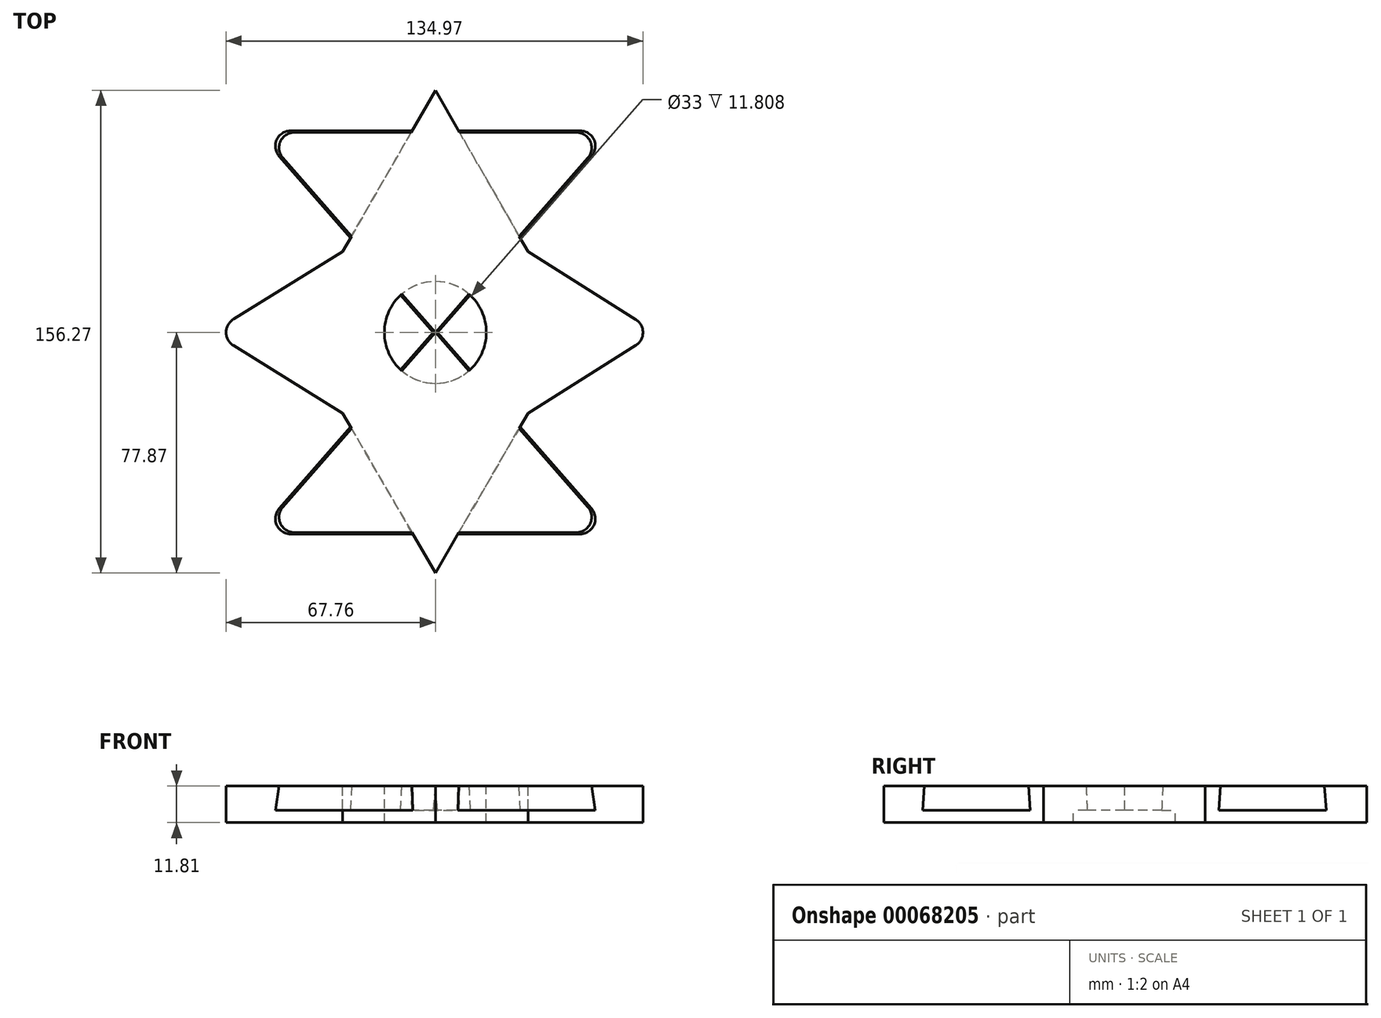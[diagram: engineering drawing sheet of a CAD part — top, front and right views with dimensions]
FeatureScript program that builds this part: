
annotation { "Feature Type Name" : "Feature", "Feature Type Description" : "" }
export const myFeature = defineFeature(function(context is Context, id is Id, definition is map)
    precondition{}
    {
        {
            var Q0;
            Q0=qCreatedBy(makeId("Top.planeOp"),FACE);
            var sketch = newSketch(context, id + "F0", { "sketchPlane" : qUnion([Q0])});
            skLineSegment(sketch, "E0.bottom", {"start": v(-30, 26.17) * mm, "end": v(30, 26.17) * mm});
            skLineSegment(sketch, "E0.top", {"start": v(-30, -26.17) * mm, "end": v(30, -26.17) * mm});
            skLineSegment(sketch, "E0.left", {"start": v(-30, 26.17) * mm, "end": v(-30, -26.17) * mm});
            skLineSegment(sketch, "E0.right", {"start": v(30, 26.17) * mm, "end": v(30, -26.17) * mm});
            skPoint(sketch, "E0.middle", {"position": v(0, 0) * mm});
            skLineSegment(sketch, "E1", {"start": v(-30, 26.17) * mm, "end": v(0, 78.4) * mm});
            skLineSegment(sketch, "E2", {"start": v(0, 78.4) * mm, "end": v(30, 26.17) * mm});
            skLineSegment(sketch, "E3", {"start": v(30, 26.17) * mm, "end": v(71.6, 0) * mm});
            skLineSegment(sketch, "E4", {"start": v(71.6, 0) * mm, "end": v(30, -26.17) * mm});
            skLineSegment(sketch, "E5", {"start": v(-30, -26.17) * mm, "end": v(-72.26, 0) * mm});
            skLineSegment(sketch, "E6", {"start": v(-72.26, 0) * mm, "end": v(-30, 26.17) * mm});
            skLineSegment(sketch, "E7", {"start": v(-30, -26.17) * mm, "end": v(0, -77.87) * mm});
            skLineSegment(sketch, "E8", {"start": v(0, -77.87) * mm, "end": v(30, -26.17) * mm});
            skCircle(sketch, "E9", {"center": v(0, 0) * mm, "radius": 16.5 * mm});
            skSolve(sketch);
        }
        {
            var Q0;
            Q0 = qSketchRegion(id + "F0", true);
            extrude(context, id + "F1", {"entities" : qUnion([Q0]), "oppositeDirection" : true, "depth" : 11.8 * mm});
        }
        {
            var Q0;
            Q0=qCreatedBy(makeId("Top.planeOp"),FACE);
            var sketch = newSketch(context, id + "F2", { "sketchPlane" : qUnion([Q0])});
            skLineSegment(sketch, "E10", {"start": v(0, 0) * mm, "end": v(-56.59, 64.76) * mm});
            skLineSegment(sketch, "E11", {"start": v(-56.59, 64.76) * mm, "end": v(56.59, 64.76) * mm});
            skLineSegment(sketch, "E12", {"start": v(56.59, 64.76) * mm, "end": v(0, 0) * mm});
            skLineSegment(sketch, "E13", {"start": v(0, 0) * mm, "end": v(-56.59, -64.76) * mm});
            skLineSegment(sketch, "E14", {"start": v(-56.59, -64.76) * mm, "end": v(56.59, -64.76) * mm});
            skLineSegment(sketch, "E15", {"start": v(56.59, -64.76) * mm, "end": v(0, 0) * mm});
            skSolve(sketch);
        }
        {
            var Q0;
            Q0=makeQuery(id+"F2.imprint","IMPRINT",FACE,{"disambiguationData":[TD([[makeQuery(id+"F2.imprint","IMPRINT",EDGE,{"derivedFrom":sQuery(id+"F2.wireOp",EDGE,"E13")}),1.0]])]});
            var Q1;
            Q1=makeQuery(id+"F2.imprint","IMPRINT",FACE,{"disambiguationData":[TD([[makeQuery(id+"F2.imprint","IMPRINT",EDGE,{"derivedFrom":sQuery(id+"F2.wireOp",EDGE,"E10")}),-1.0]])]});
            extrude(context, id + "F3", {"entities" : qUnion([Q0, Q1]), "operationType" : NewBodyOperationType.ADD, "oppositeDirection" : true, "depth" : 7.77 * mm, "hasDraft" : true, "draftAngle" : 4 * degree});
        }
        {
            var Q0;
            Q0=makeQuery(id+"F3.opExtrude","SWEPT_EDGE",EDGE,{"disambiguationData":[OSD([sQuery(id+"F2.wireOp",EDGE,"E10"),sQuery(id+"F2.wireOp",EDGE,"E11")])]});
            var Q1;
            Q1=makeQuery(id+"F1.opExtrude","SWEPT_EDGE",EDGE,{"disambiguationData":[OSD([sQuery(id+"F0.wireOp",EDGE,"E5"),sQuery(id+"F0.wireOp",EDGE,"E6")])]});
            var Q2;
            Q2=makeQuery(id+"F3.opExtrude","SWEPT_EDGE",EDGE,{"disambiguationData":[OSD([sQuery(id+"F2.wireOp",EDGE,"E13"),sQuery(id+"F2.wireOp",EDGE,"E14")])]});
            fillet(context, id + "F4", {"entities" : qUnion([Q0, Q1, Q2]), "radius" : 5 * mm, "tangentPropagation" : true, "allowEdgeOverflow" : false});
        }
        {
            var Q0;
            Q0=makeQuery(id+"F3.opExtrude","SWEPT_EDGE",EDGE,{"disambiguationData":[OSD([sQuery(id+"F2.wireOp",EDGE,"E11"),sQuery(id+"F2.wireOp",EDGE,"E12")])]});
            var Q1;
            Q1=makeQuery(id+"F1.opExtrude","SWEPT_EDGE",EDGE,{"disambiguationData":[OSD([sQuery(id+"F0.wireOp",EDGE,"E3"),sQuery(id+"F0.wireOp",EDGE,"E4")])]});
            var Q2;
            Q2=makeQuery(id+"F3.opExtrude","SWEPT_EDGE",EDGE,{"disambiguationData":[OSD([sQuery(id+"F2.wireOp",EDGE,"E14"),sQuery(id+"F2.wireOp",EDGE,"E15")])]});
            fillet(context, id + "F5", {"entities" : qUnion([Q0, Q1, Q2]), "radius" : 5 * mm, "tangentPropagation" : true, "allowEdgeOverflow" : false});
        }
    });
